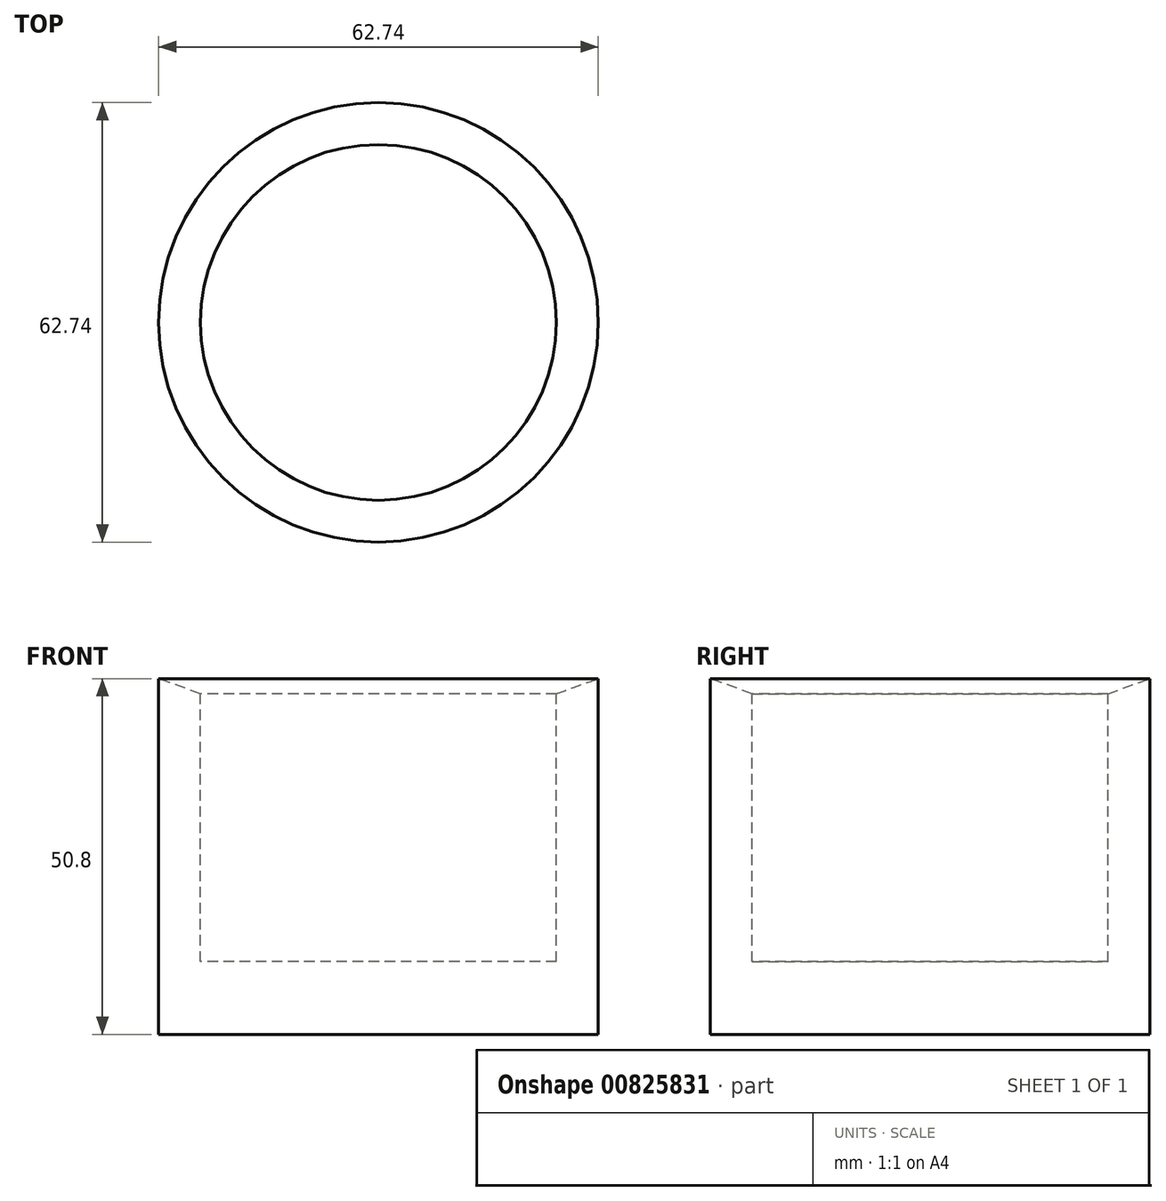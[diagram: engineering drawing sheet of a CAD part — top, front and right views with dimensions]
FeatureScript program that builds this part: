
annotation { "Feature Type Name" : "Feature", "Feature Type Description" : "" }
export const myFeature = defineFeature(function(context is Context, id is Id, definition is map)
    precondition{}
    {
        {
            var Q0;
            Q0=qCreatedBy(makeId("Front.planeOp"),FACE);
            var sketch = newSketch(context, id + "F0", { "sketchPlane" : qUnion([Q0])});
            skLineSegment(sketch, "E0", {"start": v(0, 0) * mm, "end": v(-31.37, 0) * mm});
            skLineSegment(sketch, "E1", {"start": v(-31.37, 0) * mm, "end": v(-31.37, 50.8) * mm});
            skLineSegment(sketch, "E2", {"start": v(-31.37, 50.8) * mm, "end": v(-25.4, 48.64) * mm});
            skLineSegment(sketch, "E3", {"start": v(-25.4, 48.64) * mm, "end": v(-25.4, 10.37) * mm});
            skLineSegment(sketch, "E4", {"start": v(-25.4, 10.37) * mm, "end": v(0, 10.37) * mm});
            skLineSegment(sketch, "E5", {"start": v(0, 10.37) * mm, "end": v(0, 0) * mm});
            skSolve(sketch);
        }
        {
            var Q0;
            Q0=makeQuery(id+"F0.imprint","IMPRINT",FACE,{"disambiguationData":[TD([[makeQuery(id+"F0.imprint","IMPRINT",EDGE,{"derivedFrom":sQuery(id+"F0.wireOp",EDGE,"E0")}),-1.0]])]});
            var Q1;
            Q1=sQuery(id+"F0.wireOp",EDGE,"E5");
            revolve(context, id + "F1", {"surfaceOperationType" : NewSurfaceOperationType.NEW, "entities" : qUnion([Q0]), "axis" : qUnion([Q1]), "revolveType" : RevolveType.FULL});
        }
    });
